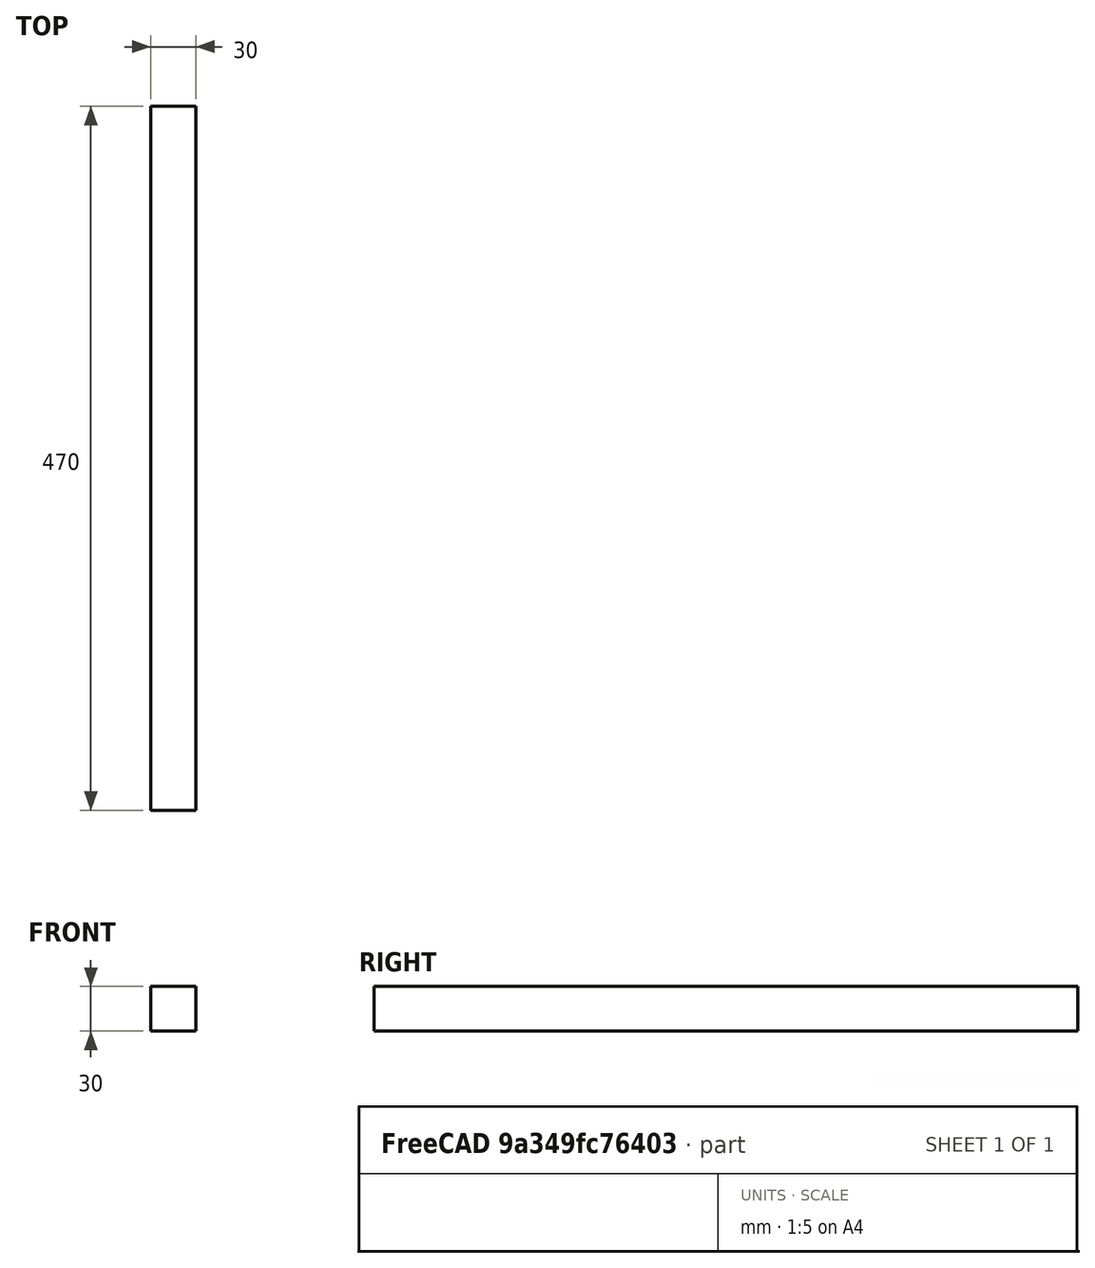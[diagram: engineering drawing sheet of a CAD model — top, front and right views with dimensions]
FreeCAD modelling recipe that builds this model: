
FCSTD DOCUMENT  (FreeCAD 0.16R6348 (Git))
Label: ChasisCentral1
License: All rights reserved
LicenseURL: http://es.wikipedia.org/wiki/Todos_los_derechos_reservados
objects: Sketcher::SketchObject×1, PartDesign::Pad×1, Part::Feature×1
note: 4 computed .brp shape members not serialized (recipe doc carries the construction recipe); baked Part::Feature solids carry a one-line shape summary decoded from their .brp

FEATURE [Sketcher::SketchObject] Sketch
  Placement = pos=(0,0,0) rot=(-1,0,0;4.71239rad)
  sketch-geometry (4):
    g0: LineSegment StartX=0 StartY=0 StartZ=0 EndX=30 EndY=0 EndZ=0
    g1: LineSegment StartX=30 StartY=0 StartZ=0 EndX=30 EndY=30 EndZ=0
    g2: LineSegment StartX=30 StartY=30 StartZ=0 EndX=0 EndY=30 EndZ=0
    g3: LineSegment StartX=0 StartY=30 StartZ=0 EndX=0 EndY=0 EndZ=0
  constraints (8):
    c: Coincident(g0,g1)
    c: Coincident(g1,g2)
    c: Coincident(g2,g3)
    c: Coincident(g3,g0)
    c: Horizontal(g0)
    c: Horizontal(g2)
    c: Vertical(g1)
    c: Vertical(g3)
FEATURE [PartDesign::Pad] Pad
  Length = 470
  Length2 = 100
  Placement = pos=(0,0,0) rot=(-1,0,0;4.71239rad)
  Sketch = -> Sketch
  Type = 0
FEATURE [Part::Feature] Pad001
  Placement = pos=(0,0,0) rot=(1,0,0;1.5708rad)
  shape: bbox 30 x 470 x 30 mm, 6 faces (baked)
